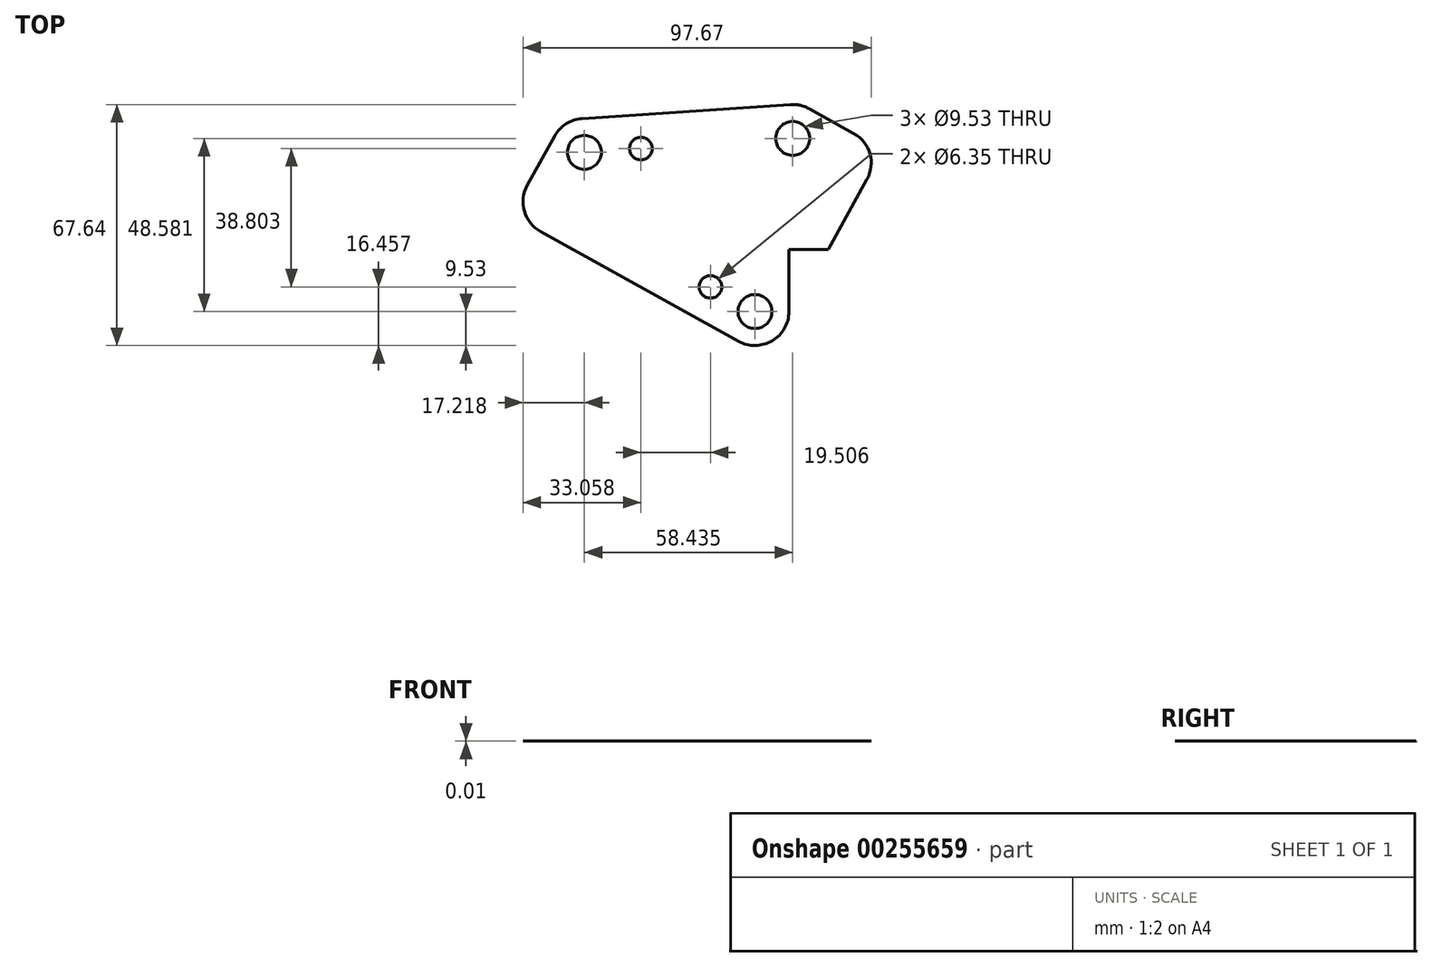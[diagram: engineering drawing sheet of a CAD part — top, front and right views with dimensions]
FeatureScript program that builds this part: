
annotation { "Feature Type Name" : "Feature", "Feature Type Description" : "" }
export const myFeature = defineFeature(function(context is Context, id is Id, definition is map)
    precondition{}
    {
        {
            var Q0;
            Q0=qCreatedBy(makeId("Top.planeOp"),FACE);
            var sketch = newSketch(context, id + "F0", { "sketchPlane" : qUnion([Q0])});
            skArc(sketch, "E0", {"start": v(-4.62, -8.33) * mm, "mid": v(4.83, -8.2) * mm, "end": v(9.53, 0) * mm});
            skLineSegment(sketch, "E1", {"start": v(0, 0) * mm, "end": v(-55.54, 30.79) * mm, "construction": true});
            skArc(sketch, "E2", {"start": v(-63.87, 35.4) * mm, "mid": v(-64.7, 28.16) * mm, "end": v(-60.16, 22.45) * mm});
            skLineSegment(sketch, "E3", {"start": v(-55.54, 30.79) * mm, "end": v(-47.84, 44.67) * mm, "construction": true});
            skArc(sketch, "E4", {"start": v(-48.48, 54.17) * mm, "mid": v(-52.95, 52.71) * mm, "end": v(-56.17, 49.29) * mm});
            skLineSegment(sketch, "E5", {"start": v(0, 0) * mm, "end": v(23.09, 41.65) * mm, "construction": true});
            skArc(sketch, "E6", {"start": v(31.42, 37.04) * mm, "mid": v(32.25, 44.28) * mm, "end": v(27.7, 49.98) * mm});
            skLineSegment(sketch, "E7", {"start": v(23.09, 41.65) * mm, "end": v(10.6, 48.58) * mm, "construction": true});
            skArc(sketch, "E8", {"start": v(15.21, 56.91) * mm, "mid": v(12.67, 57.88) * mm, "end": v(9.96, 58.08) * mm});
            skLineSegment(sketch, "E9", {"start": v(-47.84, 44.67) * mm, "end": v(10.6, 48.58) * mm, "construction": true});
            skLineSegment(sketch, "E10", {"start": v(-47.84, 44.67) * mm, "end": v(-32, 45.73) * mm});
            skLineSegment(sketch, "E11", {"start": v(0, 0) * mm, "end": v(-12.5, 6.93) * mm});
            skCircle(sketch, "E12", {"center": v(-12.5, 6.93) * mm, "radius": 3.18 * mm});
            skCircle(sketch, "E13", {"center": v(-32, 45.73) * mm, "radius": 3.18 * mm});
            skLineSegment(sketch, "E14", {"start": v(9.53, 0) * mm, "end": v(9.53, 17.46) * mm});
            skLineSegment(sketch, "E15", {"start": v(10.6, 48.58) * mm, "end": v(9.96, 58.08) * mm, "construction": true});
            skLineSegment(sketch, "E16", {"start": v(-47.84, 44.67) * mm, "end": v(-48.48, 54.17) * mm, "construction": true});
            skLineSegment(sketch, "E17", {"start": v(-48.48, 54.17) * mm, "end": v(9.96, 58.08) * mm});
            skLineSegment(sketch, "E18", {"start": v(0, 0) * mm, "end": v(-4.62, -8.33) * mm, "construction": true});
            skLineSegment(sketch, "E19", {"start": v(-55.54, 30.79) * mm, "end": v(-60.16, 22.45) * mm, "construction": true});
            skLineSegment(sketch, "E20", {"start": v(-60.16, 22.45) * mm, "end": v(-4.62, -8.33) * mm});
            skLineSegment(sketch, "E21", {"start": v(-55.54, 30.79) * mm, "end": v(-63.87, 35.4) * mm, "construction": true});
            skLineSegment(sketch, "E22", {"start": v(-47.84, 44.67) * mm, "end": v(-56.17, 49.29) * mm, "construction": true});
            skLineSegment(sketch, "E23", {"start": v(-63.87, 35.4) * mm, "end": v(-56.17, 49.29) * mm});
            skLineSegment(sketch, "E24", {"start": v(10.6, 48.58) * mm, "end": v(15.21, 56.91) * mm, "construction": true});
            skLineSegment(sketch, "E25", {"start": v(23.09, 41.65) * mm, "end": v(27.7, 49.98) * mm, "construction": true});
            skLineSegment(sketch, "E26", {"start": v(15.21, 56.91) * mm, "end": v(27.7, 49.98) * mm});
            skLineSegment(sketch, "E27", {"start": v(23.09, 41.65) * mm, "end": v(31.42, 37.04) * mm, "construction": true});
            skLineSegment(sketch, "E28", {"start": v(9.53, 17.46) * mm, "end": v(20.57, 17.46) * mm});
            skLineSegment(sketch, "E29", {"start": v(31.42, 37.04) * mm, "end": v(20.57, 17.46) * mm});
            skLineSegment(sketch, "E30", {"start": v(20.57, 17.46) * mm, "end": v(9.53, 17.46) * mm});
            skCircle(sketch, "E31", {"center": v(0, 0) * mm, "radius": 4.76 * mm});
            skCircle(sketch, "E32", {"center": v(10.6, 48.58) * mm, "radius": 4.76 * mm});
            skCircle(sketch, "E33", {"center": v(-47.84, 44.67) * mm, "radius": 4.76 * mm});
            skSolve(sketch);
        }
        {
            var Q0;
            Q0=makeQuery(id+"F0.imprint","IMPRINT",FACE,{"disambiguationData":[TD([[makeQuery(id+"F0.imprint","IMPRINT",EDGE,{"derivedFrom":sQuery(id+"F0.wireOp",EDGE,"E0")}),1.0]])]});
            extrude(context, id + "F1", {"entities" : qUnion([Q0]), "depth" : 3 / 406.4 * mm});
        }
    });
